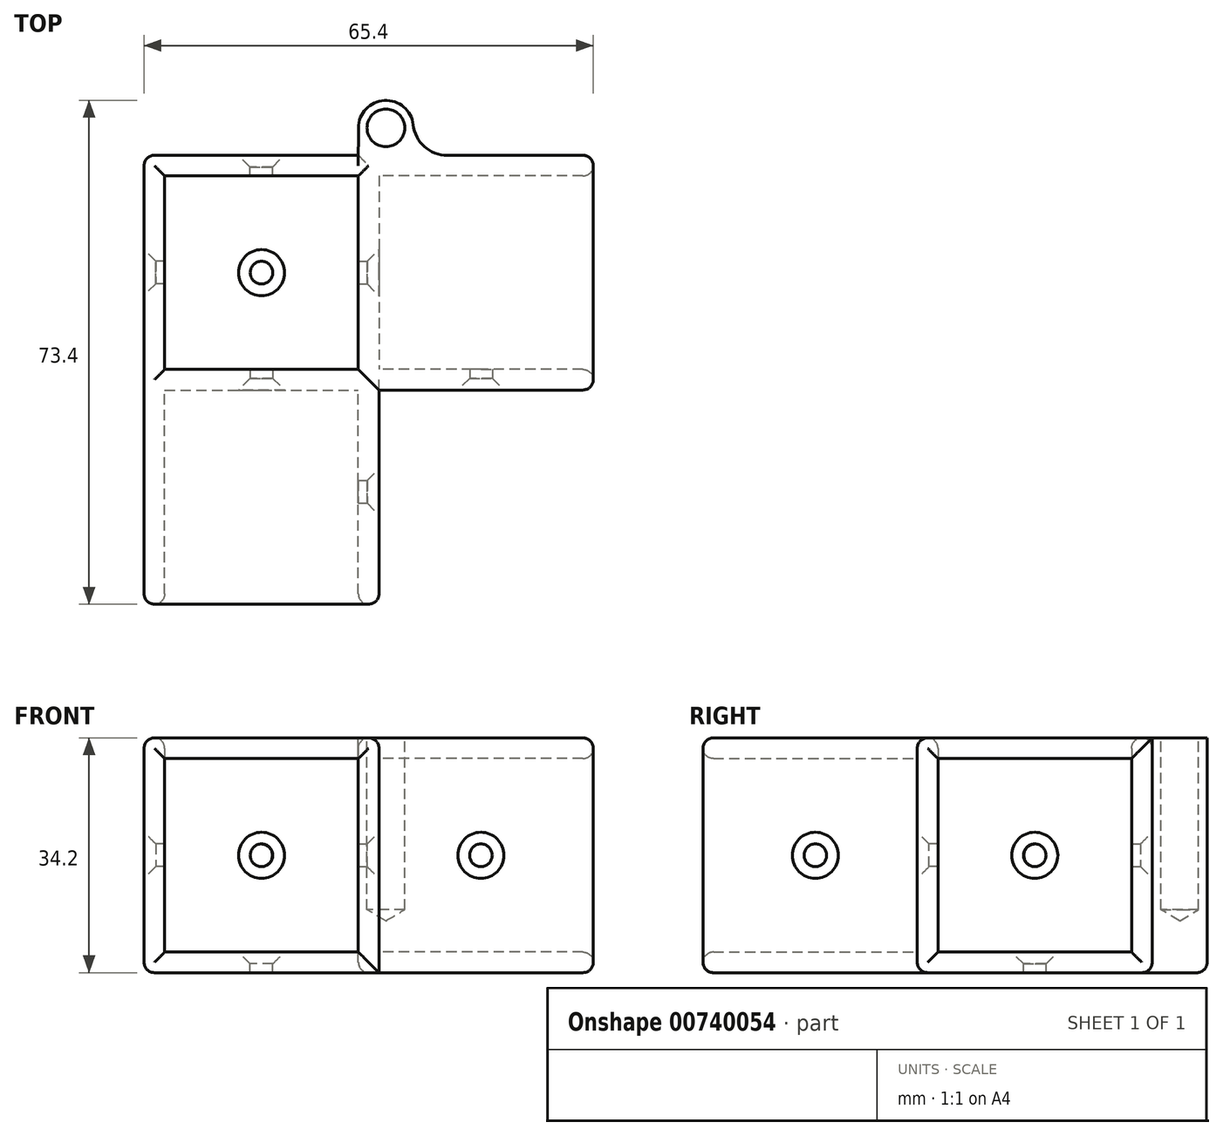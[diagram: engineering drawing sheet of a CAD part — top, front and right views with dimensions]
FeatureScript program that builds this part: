
annotation { "Feature Type Name" : "Feature", "Feature Type Description" : "" }
export const myFeature = defineFeature(function(context is Context, id is Id, definition is map)
    precondition{}
    {
        {
            var Q0;
            Q0=qCreatedBy(makeId("Top.planeOp"),FACE);
            var sketch = newSketch(context, id + "F0", { "sketchPlane" : qUnion([Q0])});
            skLineSegment(sketch, "E0.bottom", {"start": v(0, 0) * mm, "end": v(-28.2, 0) * mm});
            skLineSegment(sketch, "E0.top", {"start": v(0, 28.2) * mm, "end": v(-28.2, 28.2) * mm});
            skLineSegment(sketch, "E0.left", {"start": v(0, 0) * mm, "end": v(0, 28.2) * mm});
            skLineSegment(sketch, "E0.right", {"start": v(-28.2, 0) * mm, "end": v(-28.2, 28.2) * mm});
            skLineSegment(sketch, "E1.0", {"start": v(3, 31.2) * mm, "end": v(-31.2, 31.2) * mm});
            skLineSegment(sketch, "E1.1", {"start": v(3, -3) * mm, "end": v(3, 31.2) * mm});
            skLineSegment(sketch, "E1.2", {"start": v(3, -3) * mm, "end": v(-31.2, -3) * mm});
            skLineSegment(sketch, "E1.3", {"start": v(-31.2, -3) * mm, "end": v(-31.2, 31.2) * mm});
            skPoint(sketch, "E2", {"position": v(-14.1, 14.1) * mm});
            skSolve(sketch);
        }
        {
            var Q0;
            Q0=makeQuery(id+"F0.imprint","IMPRINT",FACE,{"disambiguationData":[TD([[makeQuery(id+"F0.imprint","IMPRINT",EDGE,{"derivedFrom":sQuery(id+"F0.wireOp",EDGE,"E0.bottom")}),1.0]])]});
            var Q1;
            Q1=makeQuery(id+"F0.imprint","IMPRINT",FACE,{"disambiguationData":[TD([[makeQuery(id+"F0.imprint","IMPRINT",EDGE,{"derivedFrom":sQuery(id+"F0.wireOp",EDGE,"E0.bottom")}),-1.0]])]});
            extrude(context, id + "F1", {"entities" : qUnion([Q0, Q1]), "oppositeDirection" : true, "depth" : 3 * mm, "offsetDistance" : 25 * mm});
        }
        {
            var Q0;
            Q0=makeQuery(id+"F0.imprint","IMPRINT",FACE,{"disambiguationData":[TD([[makeQuery(id+"F0.imprint","IMPRINT",EDGE,{"derivedFrom":sQuery(id+"F0.wireOp",EDGE,"E0.bottom")}),1.0]])]});
            extrude(context, id + "F2", {"entities" : qUnion([Q0]), "operationType" : NewBodyOperationType.ADD, "depth" : 31.2 * mm, "offsetDistance" : 25 * mm});
        }
        {
            var Q0;
            {var subQ0=sQuery(id+"F0.wireOp",EDGE,"E1.2");Q0=makeQuery(id+"F2.boolean.opBoolean","MERGE",FACE,{"derivedFrom":[makeQuery(id+"F1.opExtrude","SWEPT_FACE",FACE,{"disambiguationData":[OSD([subQ0])]}),makeQuery(id+"F2.opExtrude","SWEPT_FACE",FACE,{"disambiguationData":[OSD([subQ0])]})]});}
            var sketch = newSketch(context, id + "F3", { "sketchPlane" : qUnion([Q0])});
            skLineSegment(sketch, "E3.bottom", {"start": v(-31.2, 31.2) * mm, "end": v(3, 31.2) * mm});
            skLineSegment(sketch, "E3.top", {"start": v(-31.2, -3) * mm, "end": v(3, -3) * mm});
            skLineSegment(sketch, "E3.left", {"start": v(-31.2, 31.2) * mm, "end": v(-31.2, -3) * mm});
            skLineSegment(sketch, "E3.right", {"start": v(3, 31.2) * mm, "end": v(3, -3) * mm});
            skLineSegment(sketch, "E4.0", {"start": v(-28.2, 28.2) * mm, "end": v(0, 28.2) * mm});
            skLineSegment(sketch, "E4.1", {"start": v(-28.2, 28.2) * mm, "end": v(-28.2, 0) * mm});
            skLineSegment(sketch, "E4.2", {"start": v(-28.2, 0) * mm, "end": v(0, 0) * mm});
            skLineSegment(sketch, "E4.3", {"start": v(0, 28.2) * mm, "end": v(0, 0) * mm});
            skPoint(sketch, "E5", {"position": v(-14.1, 14.1) * mm});
            skSolve(sketch);
        }
        {
            var Q0;
            Q0=makeQuery(id+"F3.imprint","IMPRINT",FACE,{"disambiguationData":[TD([[makeQuery(id+"F3.imprint","IMPRINT",EDGE,{"derivedFrom":sQuery(id+"F3.wireOp",EDGE,"E3.bottom")}),1.0]])]});
            extrude(context, id + "F4", {"entities" : qUnion([Q0]), "operationType" : NewBodyOperationType.ADD, "depth" : 31.2 * mm, "offsetDistance" : 25 * mm});
        }
        {
            var Q0;
            {var subQ0=sQuery(id+"F0.wireOp",EDGE,"E1.1");Q0=makeQuery(id+"F4.boolean.opBoolean","MERGE",FACE,{"derivedFrom":[makeQuery(id+"F2.boolean.opBoolean","MERGE",FACE,{"derivedFrom":[makeQuery(id+"F1.opExtrude","SWEPT_FACE",FACE,{"disambiguationData":[OSD([subQ0])]}),makeQuery(id+"F2.opExtrude","SWEPT_FACE",FACE,{"disambiguationData":[OSD([subQ0])]})]}),makeQuery(id+"F4.opExtrude","SWEPT_FACE",FACE,{"disambiguationData":[OSD([sQuery(id+"F3.wireOp",EDGE,"E3.right")])]})]});}
            var sketch = newSketch(context, id + "F5", { "sketchPlane" : qUnion([Q0])});
            skLineSegment(sketch, "E6.bottom", {"start": v(31.2, 31.2) * mm, "end": v(-3, 31.2) * mm});
            skLineSegment(sketch, "E6.top", {"start": v(31.2, -3) * mm, "end": v(-3, -3) * mm});
            skLineSegment(sketch, "E6.left", {"start": v(31.2, 31.2) * mm, "end": v(31.2, -3) * mm});
            skLineSegment(sketch, "E6.right", {"start": v(-3, 31.2) * mm, "end": v(-3, -3) * mm});
            skLineSegment(sketch, "E7.0", {"start": v(28.2, 28.2) * mm, "end": v(0, 28.2) * mm});
            skLineSegment(sketch, "E7.1", {"start": v(28.2, 28.2) * mm, "end": v(28.2, 0) * mm});
            skLineSegment(sketch, "E7.2", {"start": v(28.2, 0) * mm, "end": v(0, 0) * mm});
            skLineSegment(sketch, "E7.3", {"start": v(0, 28.2) * mm, "end": v(0, 0) * mm});
            skPoint(sketch, "E8", {"position": v(14.1, 14.1) * mm});
            skSolve(sketch);
        }
        {
            var Q0;
            Q0=qSketchRegion(id+"F5",true);
            extrude(context, id + "F6", {"entities" : qUnion([Q0]), "operationType" : NewBodyOperationType.ADD, "depth" : 31.2 * mm, "offsetDistance" : 25 * mm});
        }
        {
            var Q0;
            Q0=sQuery(id+"F5.wireOp",VERTEX,"E8");
            var Q1;
            Q1=sQuery(id+"F3.wireOp",VERTEX,"E5");
            var Q2;
            Q2=makeQuery(id+"F1.opExtrude","SWEPT_BODY",BODY,{"disambiguationData":[OSD([sQuery(id+"F0.wireOp",EDGE,"E1.0"),sQuery(id+"F0.wireOp",EDGE,"E1.1"),sQuery(id+"F0.wireOp",EDGE,"E1.2"),sQuery(id+"F0.wireOp",EDGE,"E1.3")])]});
            hole(context, id + "F7", {"style" : HoleStyle.C_SINK, "endStyle" : HoleEndStyle.BLIND, "standardTappedOrClearance" : lookupTablePath({ "standard" : "ISO", "fit" : "Normal", "size" : "M3", "type" : "Clearance" }), "standardBlindInLast" : lookupTablePath({ "fit" : "Standard", "standard" : "ISO", "size" : "M3", "type" : "Clearance" }), "holeDiameter" : 3.3 * mm, "cSinkDiameter" : 6.72 * mm, "cSinkAngle" : 90 * degree, "majorDiameter" : 5 * mm, "holeDepth" : 13.5 * mm, "isTappedThrough" : true, "tappedDepth" : 12 * mm, "tapClearance" : 3, "startFromSketch" : true, "locations" : qUnion([Q0, Q1]), "scope" : qUnion([Q2])});
        }
        {
            var Q0;
            {var subQ0=sQuery(id+"F3.wireOp",EDGE,"E3.bottom");var subQ3=sQuery(id+"F0.wireOp",EDGE,"E1.1");var subQ5=sQuery(id+"F3.wireOp",EDGE,"E3.right");Q0=makeQuery(id+"F6.boolean.opBoolean","SPLIT",FACE,{"disambiguationData":[TD([makeQuery(id+"F4.opExtrude","SWEPT_FACE",FACE,{"disambiguationData":[OSD([subQ0])]})])],"derivedFrom":makeQuery(id+"F4.boolean.opBoolean","MERGE",FACE,{"derivedFrom":[makeQuery(id+"F2.boolean.opBoolean","MERGE",FACE,{"derivedFrom":[makeQuery(id+"F1.opExtrude","SWEPT_FACE",FACE,{"disambiguationData":[OSD([subQ3])]}),makeQuery(id+"F2.opExtrude","SWEPT_FACE",FACE,{"disambiguationData":[OSD([subQ3])]})]}),makeQuery(id+"F4.opExtrude","SWEPT_FACE",FACE,{"disambiguationData":[OSD([subQ5])]})]})});}
            var sketch = newSketch(context, id + "F8", { "sketchPlane" : qUnion([Q0])});
            skPoint(sketch, "E9", {"position": v(-17.85, 14.1) * mm});
            skSolve(sketch);
        }
        {
            var Q0;
            Q0=makeQuery(id+"F6.opExtrude","SWEPT_FACE",FACE,{"disambiguationData":[OSD([sQuery(id+"F5.wireOp",EDGE,"E6.right")])]});
            var sketch = newSketch(context, id + "F9", { "sketchPlane" : qUnion([Q0])});
            skPoint(sketch, "E10", {"position": v(17.85, 14.1) * mm});
            skSolve(sketch);
        }
        {
            var Q0;
            Q0=sQuery(id+"F9.wireOp",VERTEX,"E10");
            var Q1;
            Q1=sQuery(id+"F8.wireOp",VERTEX,"E9");
            var Q2;
            Q2=makeQuery(id+"F1.opExtrude","SWEPT_BODY",BODY,{"disambiguationData":[OSD([sQuery(id+"F0.wireOp",EDGE,"E1.0"),sQuery(id+"F0.wireOp",EDGE,"E1.1"),sQuery(id+"F0.wireOp",EDGE,"E1.2"),sQuery(id+"F0.wireOp",EDGE,"E1.3")])]});
            hole(context, id + "F10", {"style" : HoleStyle.C_SINK, "endStyle" : HoleEndStyle.BLIND, "standardTappedOrClearance" : lookupTablePath({ "standard" : "ISO", "fit" : "Normal", "size" : "M3", "type" : "Clearance" }), "standardBlindInLast" : lookupTablePath({ "fit" : "Standard", "standard" : "ISO", "size" : "M3", "type" : "Clearance" }), "holeDiameter" : 3.3 * mm, "cSinkDiameter" : 6.72 * mm, "cSinkAngle" : 90 * degree, "majorDiameter" : 5 * mm, "holeDepth" : 13.5 * mm, "isTappedThrough" : true, "tappedDepth" : 12 * mm, "tapClearance" : 3, "startFromSketch" : true, "locations" : qUnion([Q0, Q1]), "scope" : qUnion([Q2])});
        }
        {
            var Q0;
            {var subQ0=sQuery(id+"F0.wireOp",EDGE,"E1.0");Q0=makeQuery(id+"F6.boolean.opBoolean","MERGE",FACE,{"derivedFrom":[makeQuery(id+"F2.boolean.opBoolean","MERGE",FACE,{"derivedFrom":[makeQuery(id+"F1.opExtrude","SWEPT_FACE",FACE,{"disambiguationData":[OSD([subQ0])]}),makeQuery(id+"F2.opExtrude","SWEPT_FACE",FACE,{"disambiguationData":[OSD([subQ0])]})]}),makeQuery(id+"F6.opExtrude","SWEPT_FACE",FACE,{"disambiguationData":[OSD([sQuery(id+"F5.wireOp",EDGE,"E6.left")])]})]});}
            var sketch = newSketch(context, id + "F11", { "sketchPlane" : qUnion([Q0])});
            skPoint(sketch, "E11", {"position": v(14.15, 14.1) * mm});
            skSolve(sketch);
        }
        {
            var Q0;
            {var subQ0=sQuery(id+"F0.wireOp",EDGE,"E1.3");Q0=makeQuery(id+"F4.boolean.opBoolean","MERGE",FACE,{"derivedFrom":[makeQuery(id+"F2.boolean.opBoolean","MERGE",FACE,{"derivedFrom":[makeQuery(id+"F1.opExtrude","SWEPT_FACE",FACE,{"disambiguationData":[OSD([subQ0])]}),makeQuery(id+"F2.opExtrude","SWEPT_FACE",FACE,{"disambiguationData":[OSD([subQ0])]})]}),makeQuery(id+"F4.opExtrude","SWEPT_FACE",FACE,{"disambiguationData":[OSD([sQuery(id+"F3.wireOp",EDGE,"E3.left")])]})]});}
            var sketch = newSketch(context, id + "F12", { "sketchPlane" : qUnion([Q0])});
            skPoint(sketch, "E12", {"position": v(-14.15, 14.1) * mm});
            skSolve(sketch);
        }
        {
            var Q0;
            Q0=sQuery(id+"F12.wireOp",VERTEX,"E12");
            var Q1;
            Q1=sQuery(id+"F11.wireOp",VERTEX,"E11");
            var Q2;
            Q2=makeQuery(id+"F1.opExtrude","SWEPT_BODY",BODY,{"disambiguationData":[OSD([sQuery(id+"F0.wireOp",EDGE,"E1.0"),sQuery(id+"F0.wireOp",EDGE,"E1.1"),sQuery(id+"F0.wireOp",EDGE,"E1.2"),sQuery(id+"F0.wireOp",EDGE,"E1.3")])]});
            hole(context, id + "F13", {"style" : HoleStyle.C_SINK, "endStyle" : HoleEndStyle.BLIND, "standardTappedOrClearance" : lookupTablePath({ "standard" : "ISO", "fit" : "Normal", "size" : "M3", "type" : "Clearance" }), "standardBlindInLast" : lookupTablePath({ "fit" : "Standard", "standard" : "ISO", "size" : "M3", "type" : "Clearance" }), "holeDiameter" : 3.3 * mm, "cSinkDiameter" : 6.72 * mm, "cSinkAngle" : 90 * degree, "majorDiameter" : 5 * mm, "holeDepth" : 13.5 * mm, "isTappedThrough" : true, "tappedDepth" : 12 * mm, "tapClearance" : 3, "startFromSketch" : true, "locations" : qUnion([Q0, Q1]), "scope" : qUnion([Q2])});
        }
        {
            var Q0;
            Q0=makeQuery(id+"F6.boolean.opBoolean","MERGE",FACE,{"derivedFrom":[makeQuery(id+"F4.boolean.opBoolean","MERGE",FACE,{"derivedFrom":[makeQuery(id+"F2.opExtrude","CAP_FACE",FACE,{"disambiguationData":[OSD([sQuery(id+"F0.wireOp",EDGE,"E0.bottom"),sQuery(id+"F0.wireOp",EDGE,"E0.top"),sQuery(id+"F0.wireOp",EDGE,"E0.left"),sQuery(id+"F0.wireOp",EDGE,"E0.right"),sQuery(id+"F0.wireOp",EDGE,"E1.0"),sQuery(id+"F0.wireOp",EDGE,"E1.1"),sQuery(id+"F0.wireOp",EDGE,"E1.2"),sQuery(id+"F0.wireOp",EDGE,"E1.3")])],"isStart":false}),makeQuery(id+"F4.opExtrude","SWEPT_FACE",FACE,{"disambiguationData":[OSD([sQuery(id+"F3.wireOp",EDGE,"E3.bottom")])]})]}),makeQuery(id+"F6.opExtrude","SWEPT_FACE",FACE,{"disambiguationData":[OSD([sQuery(id+"F5.wireOp",EDGE,"E6.bottom")])]})]});
            var sketch = newSketch(context, id + "F14", { "sketchPlane" : qUnion([Q0])});
            skArc(sketch, "E13", {"start": v(8.01, 35.2) * mm, "mid": v(4.02, 39.2) * mm, "end": v(0.01, 35.21) * mm});
            skLineSegment(sketch, "E14", {"start": v(0, 31.2) * mm, "end": v(0.01, 35.21) * mm});
            skLineSegment(sketch, "E15", {"start": v(8.01, 31.2) * mm, "end": v(8.01, 35.2) * mm});
            skSolve(sketch);
        }
        {
            var Q0;
            Q0=makeQuery(id+"F14.imprint","IMPRINT",FACE,{"disambiguationData":[TD([[makeQuery(id+"F14.imprint","IMPRINT",EDGE,{"derivedFrom":sQuery(id+"F14.wireOp",EDGE,"E13")}),1.0]])]});
            var Q1;
            Q1=makeQuery(id+"F6.boolean.opBoolean","MERGE",FACE,{"derivedFrom":[makeQuery(id+"F4.boolean.opBoolean","MERGE",FACE,{"derivedFrom":[makeQuery(id+"F1.opExtrude","CAP_FACE",FACE,{"disambiguationData":[OSD([sQuery(id+"F0.wireOp",EDGE,"E1.0"),sQuery(id+"F0.wireOp",EDGE,"E1.1"),sQuery(id+"F0.wireOp",EDGE,"E1.2"),sQuery(id+"F0.wireOp",EDGE,"E1.3")])],"isStart":false}),makeQuery(id+"F4.opExtrude","SWEPT_FACE",FACE,{"disambiguationData":[OSD([sQuery(id+"F3.wireOp",EDGE,"E3.top")])]})]}),makeQuery(id+"F6.opExtrude","SWEPT_FACE",FACE,{"disambiguationData":[OSD([sQuery(id+"F5.wireOp",EDGE,"E6.top")])]})]});
            extrude(context, id + "F15", {"entities" : qUnion([Q0]), "operationType" : NewBodyOperationType.ADD, "endBound" : BoundingType.UP_TO_SURFACE, "oppositeDirection" : true, "depth" : 25 * mm, "endBoundEntityFace" : qUnion([Q1]), "offsetDistance" : 25 * mm});
        }
        {
            var Q0;
            Q0=sQuery(id+"F14.wireOp",VERTEX,"E13.center");
            var Q1;
            Q1=makeQuery(id+"F1.opExtrude","SWEPT_BODY",BODY,{"disambiguationData":[OSD([sQuery(id+"F0.wireOp",EDGE,"E1.0"),sQuery(id+"F0.wireOp",EDGE,"E1.1"),sQuery(id+"F0.wireOp",EDGE,"E1.2"),sQuery(id+"F0.wireOp",EDGE,"E1.3")])]});
            hole(context, id + "F16", {"style" : HoleStyle.SIMPLE, "endStyle" : HoleEndStyle.BLIND, "standardTappedOrClearance" : lookupTablePath({ "standard" : "ISO", "fit" : "Normal", "size" : "M5", "type" : "Clearance" }), "standardBlindInLast" : lookupTablePath({ "fit" : "Standard", "standard" : "ISO", "size" : "M5", "type" : "Clearance" }), "holeDiameter" : 5.5 * mm, "majorDiameter" : 5 * mm, "holeDepth" : 25 * mm, "isTappedThrough" : true, "tappedDepth" : 12 * mm, "tapClearance" : 3, "startFromSketch" : true, "locations" : qUnion([Q0]), "scope" : qUnion([Q1])});
        }
        {
            var Q0;
            Q0=makeQuery(id+"F15.opExtrude","SWEPT_EDGE",EDGE,{"disambiguationData":[OSD([sQuery(id+"F0.wireOp",EDGE,"E1.0"),sQuery(id+"F5.wireOp",EDGE,"E6.bottom"),sQuery(id+"F5.wireOp",EDGE,"E6.left"),sQuery(id+"F14.wireOp",EDGE,"E14")])]});
            var Q1;
            Q1=makeQuery(id+"F15.opExtrude","SWEPT_EDGE",EDGE,{"disambiguationData":[OSD([sQuery(id+"F0.wireOp",EDGE,"E1.0"),sQuery(id+"F5.wireOp",EDGE,"E6.bottom"),sQuery(id+"F5.wireOp",EDGE,"E6.left"),sQuery(id+"F14.wireOp",EDGE,"E15")])]});
            fillet(context, id + "F17", {"entities" : qUnion([Q0, Q1]), "radius" : 5 * mm, "tangentPropagation" : true, "allowEdgeOverflow" : false});
        }
        {
            var Q0;
            {var subQ0=sQuery(id+"F5.wireOp",EDGE,"E6.left");var subQ1=sQuery(id+"F5.wireOp",EDGE,"E6.bottom");var subQ2=sQuery(id+"F0.wireOp",EDGE,"E1.3");var subQ4=sQuery(id+"F0.wireOp",EDGE,"E1.0");Q0=makeQuery(id+"F15.boolean.opBoolean","SPLIT",EDGE,{"disambiguationData":[TD([makeQuery(id+"F1.opExtrude","SWEPT_FACE",FACE,{"disambiguationData":[OSD([subQ2])]})])],"derivedFrom":makeQuery(id+"F6.boolean.opBoolean","MERGE",EDGE,{"derivedFrom":[makeQuery(id+"F2.opExtrude","CAP_EDGE",EDGE,{"disambiguationData":[OSD([subQ4])],"isStart":false}),makeQuery(id+"F6.opExtrude","SWEPT_EDGE",EDGE,{"disambiguationData":[OSD([subQ1,subQ0])]})]})});}
            var Q1;
            Q1=makeQuery(id+"F2.opExtrude","CAP_EDGE",EDGE,{"disambiguationData":[OSD([sQuery(id+"F0.wireOp",EDGE,"E0.top")])],"isStart":false});
            var Q2;
            {var subQ0=sQuery(id+"F5.wireOp",EDGE,"E6.top");var subQ2=sQuery(id+"F0.wireOp",EDGE,"E1.3");var subQ5=sQuery(id+"F0.wireOp",EDGE,"E1.0");var subQ6=sQuery(id+"F5.wireOp",EDGE,"E6.left");Q2=makeQuery(id+"F15.boolean.opBoolean","SPLIT",EDGE,{"disambiguationData":[TD([makeQuery(id+"F1.opExtrude","SWEPT_FACE",FACE,{"disambiguationData":[OSD([subQ2])]})])],"derivedFrom":makeQuery(id+"F6.boolean.opBoolean","MERGE",EDGE,{"derivedFrom":[makeQuery(id+"F1.opExtrude","CAP_EDGE",EDGE,{"disambiguationData":[OSD([subQ5])],"isStart":false}),makeQuery(id+"F6.opExtrude","SWEPT_EDGE",EDGE,{"disambiguationData":[OSD([subQ0,subQ6])]})]})});}
            var Q3;
            {var subQ1=sQuery(id+"F0.wireOp",EDGE,"E1.0");var subQ5=sQuery(id+"F5.wireOp",EDGE,"E6.left");var subQ6=sQuery(id+"F5.wireOp",EDGE,"E6.top");Q3=makeQuery(id+"F15.boolean.opBoolean","SPLIT",EDGE,{"disambiguationData":[TD([makeQuery(id+"F15.opExtrude","SWEPT_FACE",FACE,{"disambiguationData":[OSD([sQuery(id+"F14.wireOp",EDGE,"E15")])]})])],"derivedFrom":makeQuery(id+"F6.boolean.opBoolean","MERGE",EDGE,{"derivedFrom":[makeQuery(id+"F1.opExtrude","CAP_EDGE",EDGE,{"disambiguationData":[OSD([subQ1])],"isStart":false}),makeQuery(id+"F6.opExtrude","SWEPT_EDGE",EDGE,{"disambiguationData":[OSD([subQ6,subQ5])]})]})});}
            var Q4;
            Q4=makeQuery(id+"F6.opExtrude","CAP_EDGE",EDGE,{"disambiguationData":[OSD([sQuery(id+"F5.wireOp",EDGE,"E6.bottom")])],"isStart":false});
            var Q5;
            Q5=makeQuery(id+"F6.opExtrude","CAP_EDGE",EDGE,{"disambiguationData":[OSD([sQuery(id+"F5.wireOp",EDGE,"E6.left")])],"isStart":false});
            var Q6;
            Q6=makeQuery(id+"F6.opExtrude","CAP_EDGE",EDGE,{"disambiguationData":[OSD([sQuery(id+"F5.wireOp",EDGE,"E7.1")])],"isStart":false});
            var Q7;
            Q7=makeQuery(id+"F6.opExtrude","CAP_EDGE",EDGE,{"disambiguationData":[OSD([sQuery(id+"F5.wireOp",EDGE,"E7.0")])],"isStart":false});
            var Q8;
            Q8=makeQuery(id+"F6.opExtrude","CAP_EDGE",EDGE,{"disambiguationData":[OSD([sQuery(id+"F5.wireOp",EDGE,"E7.3")])],"isStart":false});
            var Q9;
            Q9=makeQuery(id+"F6.opExtrude","CAP_EDGE",EDGE,{"disambiguationData":[OSD([sQuery(id+"F5.wireOp",EDGE,"E6.right")])],"isStart":false});
            var Q10;
            Q10=makeQuery(id+"F6.opExtrude","CAP_EDGE",EDGE,{"disambiguationData":[OSD([sQuery(id+"F5.wireOp",EDGE,"E6.top")])],"isStart":false});
            var Q11;
            Q11=makeQuery(id+"F6.opExtrude","CAP_EDGE",EDGE,{"disambiguationData":[OSD([sQuery(id+"F5.wireOp",EDGE,"E7.2")])],"isStart":false});
            var Q12;
            Q12=makeQuery(id+"F6.opExtrude","SWEPT_EDGE",EDGE,{"disambiguationData":[OSD([sQuery(id+"F0.wireOp",EDGE,"E1.1"),sQuery(id+"F3.wireOp",EDGE,"E3.top"),sQuery(id+"F3.wireOp",EDGE,"E3.right"),sQuery(id+"F5.wireOp",EDGE,"E6.top"),sQuery(id+"F5.wireOp",EDGE,"E6.right")])]});
            var Q13;
            Q13=makeQuery(id+"F6.opExtrude","CAP_EDGE",EDGE,{"disambiguationData":[OSD([sQuery(id+"F5.wireOp",EDGE,"E6.right")])],"isStart":true});
            var Q14;
            Q14=makeQuery(id+"F6.opExtrude","SWEPT_EDGE",EDGE,{"disambiguationData":[OSD([sQuery(id+"F0.wireOp",EDGE,"E1.1"),sQuery(id+"F3.wireOp",EDGE,"E3.bottom"),sQuery(id+"F3.wireOp",EDGE,"E3.right"),sQuery(id+"F5.wireOp",EDGE,"E6.bottom"),sQuery(id+"F5.wireOp",EDGE,"E6.right")])]});
            var Q15;
            Q15=makeQuery(id+"F4.boolean.opBoolean","MERGE",EDGE,{"derivedFrom":[makeQuery(id+"F2.opExtrude","CAP_EDGE",EDGE,{"disambiguationData":[OSD([sQuery(id+"F0.wireOp",EDGE,"E1.1")])],"isStart":false}),makeQuery(id+"F4.opExtrude","SWEPT_EDGE",EDGE,{"disambiguationData":[OSD([sQuery(id+"F3.wireOp",EDGE,"E3.bottom"),sQuery(id+"F3.wireOp",EDGE,"E3.right")])]})]});
            var Q16;
            Q16=makeQuery(id+"F4.opExtrude","CAP_EDGE",EDGE,{"disambiguationData":[OSD([sQuery(id+"F3.wireOp",EDGE,"E3.right")])],"isStart":false});
            var Q17;
            Q17=makeQuery(id+"F4.opExtrude","CAP_EDGE",EDGE,{"disambiguationData":[OSD([sQuery(id+"F3.wireOp",EDGE,"E4.2")])],"isStart":false});
            var Q18;
            Q18=makeQuery(id+"F4.opExtrude","CAP_EDGE",EDGE,{"disambiguationData":[OSD([sQuery(id+"F3.wireOp",EDGE,"E4.3")])],"isStart":false});
            var Q19;
            Q19=makeQuery(id+"F4.opExtrude","CAP_EDGE",EDGE,{"disambiguationData":[OSD([sQuery(id+"F3.wireOp",EDGE,"E4.0")])],"isStart":false});
            var Q20;
            Q20=makeQuery(id+"F4.opExtrude","CAP_EDGE",EDGE,{"disambiguationData":[OSD([sQuery(id+"F3.wireOp",EDGE,"E4.1")])],"isStart":false});
            var Q21;
            Q21=makeQuery(id+"F4.opExtrude","CAP_EDGE",EDGE,{"disambiguationData":[OSD([sQuery(id+"F3.wireOp",EDGE,"E3.top")])],"isStart":false});
            var Q22;
            Q22=makeQuery(id+"F4.opExtrude","CAP_EDGE",EDGE,{"disambiguationData":[OSD([sQuery(id+"F3.wireOp",EDGE,"E3.bottom")])],"isStart":false});
            var Q23;
            Q23=makeQuery(id+"F4.opExtrude","CAP_EDGE",EDGE,{"disambiguationData":[OSD([sQuery(id+"F3.wireOp",EDGE,"E3.left")])],"isStart":false});
            var Q24;
            Q24=makeQuery(id+"F4.boolean.opBoolean","MERGE",EDGE,{"derivedFrom":[makeQuery(id+"F2.opExtrude","CAP_EDGE",EDGE,{"disambiguationData":[OSD([sQuery(id+"F0.wireOp",EDGE,"E1.3")])],"isStart":false}),makeQuery(id+"F4.opExtrude","SWEPT_EDGE",EDGE,{"disambiguationData":[OSD([sQuery(id+"F3.wireOp",EDGE,"E3.bottom"),sQuery(id+"F3.wireOp",EDGE,"E3.left")])]})]});
            var Q25;
            {var subQ0=sQuery(id+"F0.wireOp",EDGE,"E1.3");var subQ1=sQuery(id+"F0.wireOp",EDGE,"E1.0");Q25=makeQuery(id+"F2.boolean.opBoolean","MERGE",EDGE,{"derivedFrom":[makeQuery(id+"F1.opExtrude","SWEPT_EDGE",EDGE,{"disambiguationData":[OSD([subQ1,subQ0])]}),makeQuery(id+"F2.opExtrude","SWEPT_EDGE",EDGE,{"disambiguationData":[OSD([subQ1,subQ0])]})]});}
            var Q26;
            Q26=makeQuery(id+"F4.boolean.opBoolean","MERGE",EDGE,{"derivedFrom":[makeQuery(id+"F1.opExtrude","CAP_EDGE",EDGE,{"disambiguationData":[OSD([sQuery(id+"F0.wireOp",EDGE,"E1.3")])],"isStart":false}),makeQuery(id+"F4.opExtrude","SWEPT_EDGE",EDGE,{"disambiguationData":[OSD([sQuery(id+"F3.wireOp",EDGE,"E3.top"),sQuery(id+"F3.wireOp",EDGE,"E3.left")])]})]});
            var Q27;
            Q27=makeQuery(id+"F2.opExtrude","CAP_EDGE",EDGE,{"disambiguationData":[OSD([sQuery(id+"F0.wireOp",EDGE,"E0.left")])],"isStart":false});
            var Q28;
            Q28=makeQuery(id+"F2.opExtrude","CAP_EDGE",EDGE,{"disambiguationData":[OSD([sQuery(id+"F0.wireOp",EDGE,"E0.bottom")])],"isStart":false});
            var Q29;
            Q29=makeQuery(id+"F2.opExtrude","CAP_EDGE",EDGE,{"disambiguationData":[OSD([sQuery(id+"F0.wireOp",EDGE,"E0.right")])],"isStart":false});
            fillet(context, id + "F18", {"entities" : qUnion([Q0, Q1, Q2, Q3, Q4, Q5, Q6, Q7, Q8, Q9, Q10, Q11, Q12, Q13, Q14, Q15, Q16, Q17, Q18, Q19, Q20, Q21, Q22, Q23, Q24, Q25, Q26, Q27, Q28, Q29]), "radius" : 1.5 * mm, "tangentPropagation" : true, "allowEdgeOverflow" : false});
        }
        {
            var Q0;
            Q0=sQuery(id+"F0.wireOp",VERTEX,"E2");
            var Q1;
            Q1=makeQuery(id+"F1.opExtrude","SWEPT_BODY",BODY,{"disambiguationData":[OSD([sQuery(id+"F0.wireOp",EDGE,"E1.0"),sQuery(id+"F0.wireOp",EDGE,"E1.1"),sQuery(id+"F0.wireOp",EDGE,"E1.2"),sQuery(id+"F0.wireOp",EDGE,"E1.3")])]});
            hole(context, id + "F19", {"style" : HoleStyle.C_SINK, "endStyle" : HoleEndStyle.BLIND, "standardTappedOrClearance" : lookupTablePath({ "standard" : "ISO", "fit" : "Normal", "size" : "M3", "type" : "Clearance" }), "standardBlindInLast" : lookupTablePath({ "fit" : "Standard", "standard" : "ISO", "size" : "M3", "type" : "Clearance" }), "holeDiameter" : 3.3 * mm, "cSinkDiameter" : 6.72 * mm, "cSinkAngle" : 90 * degree, "majorDiameter" : 5 * mm, "holeDepth" : 13.5 * mm, "isTappedThrough" : true, "tappedDepth" : 12 * mm, "tapClearance" : 3, "startFromSketch" : true, "locations" : qUnion([Q0]), "scope" : qUnion([Q1])});
        }
    });
